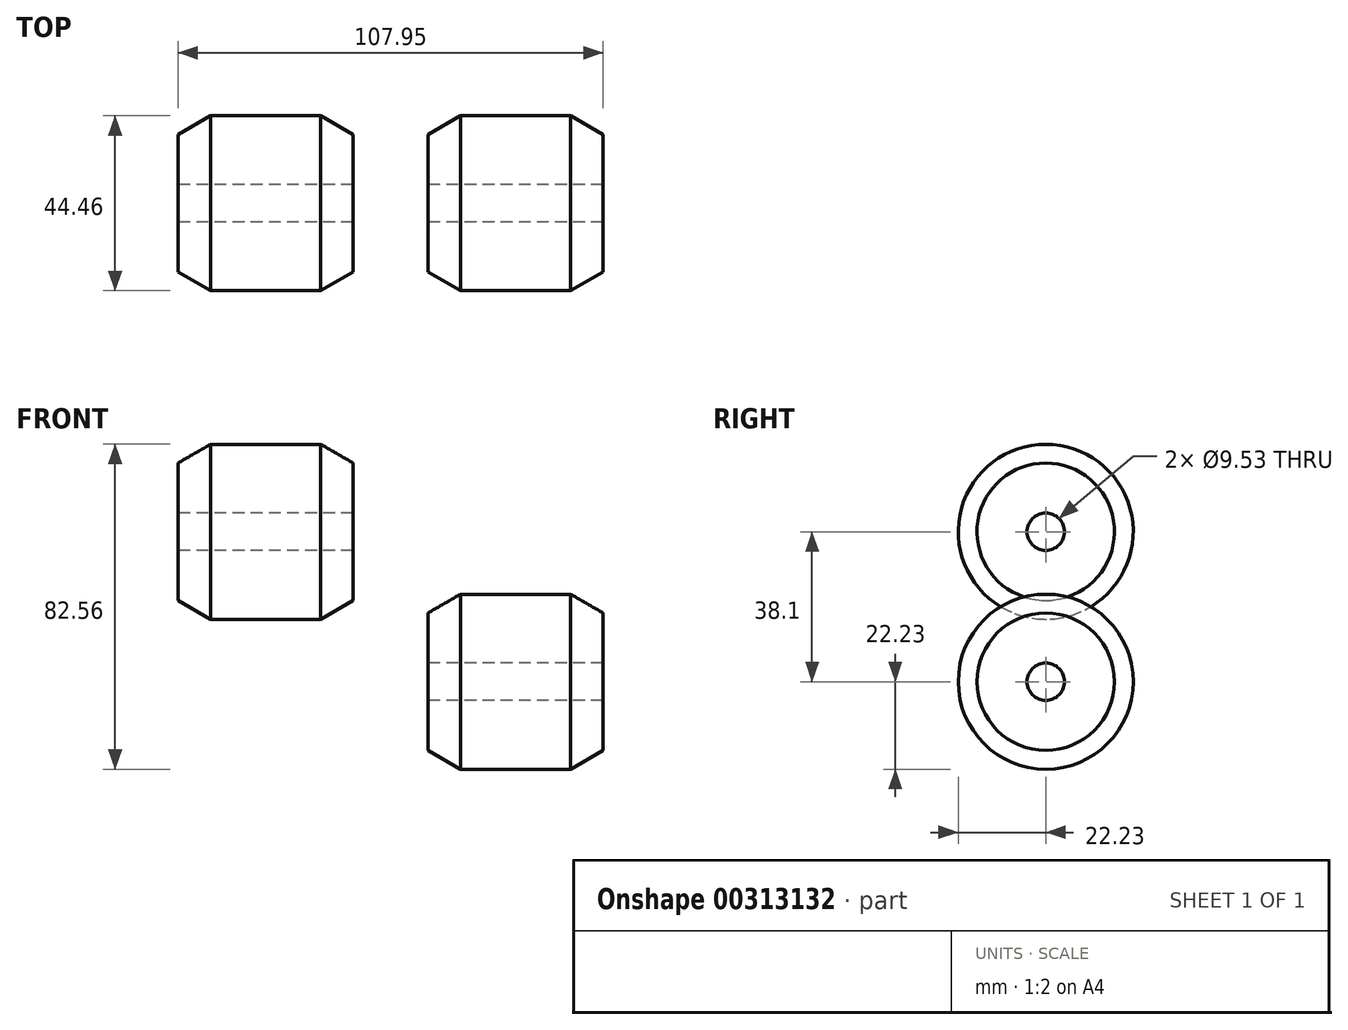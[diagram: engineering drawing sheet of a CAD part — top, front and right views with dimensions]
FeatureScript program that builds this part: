
annotation { "Feature Type Name" : "Feature", "Feature Type Description" : "" }
export const myFeature = defineFeature(function(context is Context, id is Id, definition is map)
    precondition{}
    {
        {
            var Q0;
            Q0=qCreatedBy(makeId("Front.planeOp"),FACE);
            var sketch = newSketch(context, id + "F0", { "sketchPlane" : qUnion([Q0])});
            skLineSegment(sketch, "E0", {"start": v(0, 0) * mm, "end": v(44.45, 0) * mm});
            skLineSegment(sketch, "E1", {"start": v(0, 0) * mm, "end": v(0, 17.46) * mm});
            skLineSegment(sketch, "E2", {"start": v(0, 17.46) * mm, "end": v(8.25, 22.23) * mm});
            skLineSegment(sketch, "E3", {"start": v(8.25, 22.23) * mm, "end": v(36.2, 22.23) * mm});
            skLineSegment(sketch, "E4", {"start": v(36.2, 22.22) * mm, "end": v(44.45, 17.46) * mm});
            skLineSegment(sketch, "E5", {"start": v(44.45, 17.46) * mm, "end": v(44.45, 0) * mm});
            skLineSegment(sketch, "E6", {"start": v(63.5, -38.1) * mm, "end": v(107.95, -38.1) * mm});
            skLineSegment(sketch, "E7", {"start": v(63.5, -38.1) * mm, "end": v(63.5, -20.64) * mm});
            skLineSegment(sketch, "E8", {"start": v(63.5, -20.64) * mm, "end": v(71.75, -15.88) * mm});
            skLineSegment(sketch, "E9", {"start": v(71.75, -15.88) * mm, "end": v(99.7, -15.88) * mm});
            skLineSegment(sketch, "E10", {"start": v(99.7, -15.87) * mm, "end": v(107.95, -20.64) * mm});
            skLineSegment(sketch, "E11", {"start": v(107.95, -20.64) * mm, "end": v(107.95, -38.1) * mm});
            skSolve(sketch);
        }
        {
            var Q0;
            Q0=makeQuery(id+"F0.imprint","IMPRINT",FACE,{"disambiguationData":[TD([[makeQuery(id+"F0.imprint","IMPRINT",EDGE,{"derivedFrom":sQuery(id+"F0.wireOp",EDGE,"E0")}),1.0]])]});
            var Q1;
            Q1=sQuery(id+"F0.wireOp",EDGE,"E0");
            revolve(context, id + "F1", {"entities" : qUnion([Q0]), "axis" : qUnion([Q1]), "revolveType" : RevolveType.FULL});
        }
        {
            var Q0;
            Q0=makeQuery(id+"F0.imprint","IMPRINT",FACE,{"disambiguationData":[TD([[makeQuery(id+"F0.imprint","IMPRINT",EDGE,{"derivedFrom":sQuery(id+"F0.wireOp",EDGE,"E6")}),1.0]])]});
            var Q1;
            Q1=sQuery(id+"F0.wireOp",EDGE,"E6");
            revolve(context, id + "F2", {"entities" : qUnion([Q0]), "axis" : qUnion([Q1]), "revolveType" : RevolveType.FULL});
        }
        {
            var Q0;
            Q0=makeQuery(id+"F1.opRevolve","SWEPT_FACE",FACE,{"disambiguationData":[OSD([sQuery(id+"F0.wireOp",EDGE,"E1")])]});
            var sketch = newSketch(context, id + "F3", { "sketchPlane" : qUnion([Q0])});
            skCircle(sketch, "E12", {"center": v(0, 0) * mm, "radius": 4.76 * mm});
            skCircle(sketch, "E13", {"center": v(0, -38.1) * mm, "radius": 4.76 * mm});
            skSolve(sketch);
        }
        {
            var Q0;
            Q0=qSketchRegion(id+"F3",true);
            extrude(context, id + "F4", {"entities" : qUnion([Q0]), "operationType" : NewBodyOperationType.REMOVE, "endBound" : BoundingType.THROUGH_ALL, "oppositeDirection" : true, "depth" : 25.4 * mm});
        }
    });
